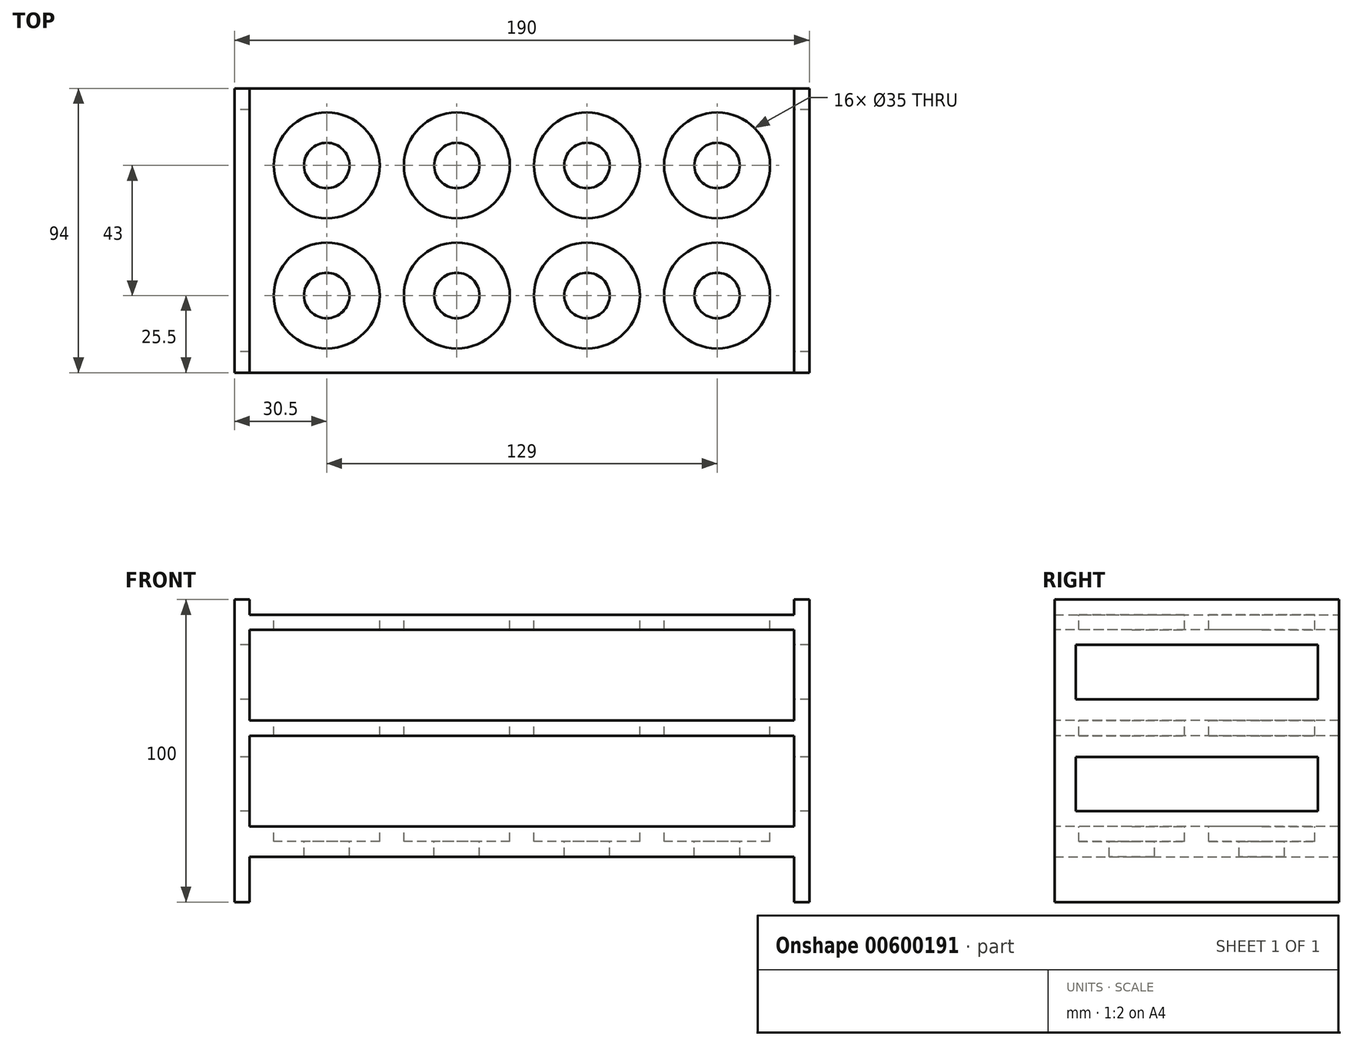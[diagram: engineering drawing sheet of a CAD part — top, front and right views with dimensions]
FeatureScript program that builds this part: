
annotation { "Feature Type Name" : "Feature", "Feature Type Description" : "" }
export const myFeature = defineFeature(function(context is Context, id is Id, definition is map)
    precondition{}
    {
        {
            var Q0;
            Q0=qCreatedBy(makeId("Top.planeOp"),FACE);
            var sketch = newSketch(context, id + "F0", { "sketchPlane" : qUnion([Q0])});
            skLineSegment(sketch, "E0.bottom", {"start": v(0, 0) * mm, "end": v(180, 0) * mm});
            skLineSegment(sketch, "E0.top", {"start": v(0, 94) * mm, "end": v(180, 94) * mm});
            skLineSegment(sketch, "E0.left", {"start": v(0, 0) * mm, "end": v(0, 94) * mm});
            skLineSegment(sketch, "E0.right", {"start": v(180, 0) * mm, "end": v(180, 94) * mm});
            skSolve(sketch);
        }
        {
            var Q0;
            Q0 = qSketchRegion(id + "F0", true);
            extrude(context, id + "F1", {"entities" : qUnion([Q0]), "depth" : 80 * mm, "offsetDistance" : 25 * mm});
        }
        {
            var Q0;
            Q0=makeQuery(id+"F1.opExtrude","CAP_FACE",FACE,{"disambiguationData":[OSD([sQuery(id+"F0.wireOp",EDGE,"E0.bottom"),sQuery(id+"F0.wireOp",EDGE,"E0.top"),sQuery(id+"F0.wireOp",EDGE,"E0.left"),sQuery(id+"F0.wireOp",EDGE,"E0.right")])],"isStart":false});
            var sketch = newSketch(context, id + "F2", { "sketchPlane" : qUnion([Q0])});
            skCircle(sketch, "E1", {"center": v(25.5, 25.5) * mm, "radius": 17.5 * mm});
            skCircle(sketch, "E2.0.1.0", {"center": v(25.5, 68.5) * mm, "radius": 17.5 * mm});
            skCircle(sketch, "E2.1.0.0", {"center": v(68.5, 25.5) * mm, "radius": 17.5 * mm});
            skCircle(sketch, "E2.1.1.0", {"center": v(68.5, 68.5) * mm, "radius": 17.5 * mm});
            skCircle(sketch, "E2.2.0.0", {"center": v(111.5, 25.5) * mm, "radius": 17.5 * mm});
            skCircle(sketch, "E2.2.1.0", {"center": v(111.5, 68.5) * mm, "radius": 17.5 * mm});
            skCircle(sketch, "E2.3.0.0", {"center": v(154.5, 25.5) * mm, "radius": 17.5 * mm});
            skCircle(sketch, "E2.3.1.0", {"center": v(154.5, 68.5) * mm, "radius": 17.5 * mm});
            skLineSegment(sketch, "E2.direction1", {"start": v(25.5, 25.5) * mm, "end": v(68.5, 25.5) * mm, "construction": true});
            skLineSegment(sketch, "E2.direction2", {"start": v(25.5, 25.5) * mm, "end": v(25.5, 68.5) * mm, "construction": true});
            skSolve(sketch);
        }
        {
            var Q0;
            Q0 = qSketchRegion(id + "F2", true);
            extrude(context, id + "F3", {"entities" : qUnion([Q0]), "operationType" : NewBodyOperationType.REMOVE, "oppositeDirection" : true, "depth" : 75 * mm, "offsetDistance" : 25 * mm});
        }
        {
            var Q0;
            Q0=makeQuery(id+"F1.opExtrude","SWEPT_FACE",FACE,{"disambiguationData":[OSD([sQuery(id+"F0.wireOp",EDGE,"E0.right")])]});
            var sketch = newSketch(context, id + "F4", { "sketchPlane" : qUnion([Q0])});
            skLineSegment(sketch, "E3.bottom", {"start": v(0, 75) * mm, "end": v(94, 75) * mm});
            skLineSegment(sketch, "E3.top", {"start": v(0, 45) * mm, "end": v(94, 45) * mm});
            skLineSegment(sketch, "E3.left", {"start": v(0, 75) * mm, "end": v(0, 45) * mm});
            skLineSegment(sketch, "E3.right", {"start": v(94, 75) * mm, "end": v(94, 45) * mm});
            skLineSegment(sketch, "E4.bottom", {"start": v(0, 40) * mm, "end": v(94, 40) * mm});
            skLineSegment(sketch, "E4.top", {"start": v(0, 10) * mm, "end": v(94, 10) * mm});
            skLineSegment(sketch, "E4.left", {"start": v(0, 40) * mm, "end": v(0, 10) * mm});
            skLineSegment(sketch, "E4.right", {"start": v(94, 40) * mm, "end": v(94, 10) * mm});
            skSolve(sketch);
        }
        {
            var Q0;
            Q0=makeQuery(id+"F4.imprint","IMPRINT",FACE,{"disambiguationData":[TD([[makeQuery(id+"F4.imprint","IMPRINT",EDGE,{"derivedFrom":sQuery(id+"F4.wireOp",EDGE,"E3.bottom")}),-1.0]])]});
            var Q1;
            Q1=makeQuery(id+"F4.imprint","IMPRINT",FACE,{"disambiguationData":[TD([[makeQuery(id+"F4.imprint","IMPRINT",EDGE,{"derivedFrom":sQuery(id+"F4.wireOp",EDGE,"E4.bottom")}),-1.0]])]});
            extrude(context, id + "F5", {"entities" : qUnion([Q0, Q1]), "operationType" : NewBodyOperationType.REMOVE, "endBound" : BoundingType.THROUGH_ALL, "oppositeDirection" : true, "depth" : 25 * mm, "offsetDistance" : 25 * mm});
        }
        {
            var Q0;
            {var subQ1=sQuery(id+"F0.wireOp",EDGE,"E0.left");Q0=makeQuery(id+"F5.boolean.opBoolean","SPLIT",FACE,{"disambiguationData":[TD([makeQuery(id+"F5.opExtrude","SWEPT_FACE",FACE,{"disambiguationData":[OSD([sQuery(id+"F4.wireOp",EDGE,"E3.bottom")])]})])],"derivedFrom":makeQuery(id+"F1.opExtrude","SWEPT_FACE",FACE,{"disambiguationData":[OSD([subQ1])]})});}
            var sketch = newSketch(context, id + "F6", { "sketchPlane" : qUnion([Q0])});
            skLineSegment(sketch, "E5.bottom", {"start": v(0, 85) * mm, "end": v(-94, 85) * mm});
            skLineSegment(sketch, "E5.top", {"start": v(0, -15) * mm, "end": v(-94, -15) * mm});
            skLineSegment(sketch, "E5.left", {"start": v(0, 85) * mm, "end": v(0, -15) * mm});
            skLineSegment(sketch, "E5.right", {"start": v(-94, 85) * mm, "end": v(-94, -15) * mm});
            skSolve(sketch);
        }
        {
            var Q0;
            Q0 = qSketchRegion(id + "F6", true);
            extrude(context, id + "F7", {"entities" : qUnion([Q0]), "operationType" : NewBodyOperationType.ADD, "depth" : 5 * mm, "offsetDistance" : 25 * mm});
        }
        {
            var Q0;
            {var subQ1=sQuery(id+"F0.wireOp",EDGE,"E0.right");Q0=makeQuery(id+"F5.boolean.opBoolean","SPLIT",FACE,{"disambiguationData":[TD([makeQuery(id+"F5.opExtrude","SWEPT_FACE",FACE,{"disambiguationData":[OSD([sQuery(id+"F4.wireOp",EDGE,"E3.bottom")])]})])],"derivedFrom":makeQuery(id+"F1.opExtrude","SWEPT_FACE",FACE,{"disambiguationData":[OSD([subQ1])]})});}
            var sketch = newSketch(context, id + "F8", { "sketchPlane" : qUnion([Q0])});
            skLineSegment(sketch, "E6.bottom", {"start": v(0, 85) * mm, "end": v(94, 85) * mm});
            skLineSegment(sketch, "E6.top", {"start": v(0, -15) * mm, "end": v(94, -15) * mm});
            skLineSegment(sketch, "E6.left", {"start": v(0, 85) * mm, "end": v(0, -15) * mm});
            skLineSegment(sketch, "E6.right", {"start": v(94, 85) * mm, "end": v(94, -15) * mm});
            skSolve(sketch);
        }
        {
            var Q0;
            Q0 = qSketchRegion(id + "F8", true);
            extrude(context, id + "F9", {"entities" : qUnion([Q0]), "operationType" : NewBodyOperationType.ADD, "depth" : 5 * mm, "offsetDistance" : 25 * mm});
        }
        {
            var Q0;
            Q0=makeQuery(id+"F3.boolean.opBoolean","COPY",FACE,{"derivedFrom":makeQuery(id+"F3.opExtrude","CAP_FACE",FACE,{"disambiguationData":[OSD([sQuery(id+"F2.wireOp",EDGE,"E1")])],"isStart":false})});
            var sketch = newSketch(context, id + "F10", { "sketchPlane" : qUnion([Q0])});
            skCircle(sketch, "E7", {"center": v(25.5, 25.5) * mm, "radius": 7.5 * mm});
            skCircle(sketch, "E8.0.1.0", {"center": v(25.5, 68.5) * mm, "radius": 7.5 * mm});
            skCircle(sketch, "E8.1.0.0", {"center": v(68.5, 25.5) * mm, "radius": 7.5 * mm});
            skCircle(sketch, "E8.1.1.0", {"center": v(68.5, 68.5) * mm, "radius": 7.5 * mm});
            skCircle(sketch, "E8.2.0.0", {"center": v(111.5, 25.5) * mm, "radius": 7.5 * mm});
            skCircle(sketch, "E8.2.1.0", {"center": v(111.5, 68.5) * mm, "radius": 7.5 * mm});
            skCircle(sketch, "E8.3.0.0", {"center": v(154.5, 25.5) * mm, "radius": 7.5 * mm});
            skCircle(sketch, "E8.3.1.0", {"center": v(154.5, 68.5) * mm, "radius": 7.5 * mm});
            skLineSegment(sketch, "E8.direction1", {"start": v(25.5, 25.5) * mm, "end": v(68.5, 25.5) * mm, "construction": true});
            skLineSegment(sketch, "E8.direction2", {"start": v(25.5, 25.5) * mm, "end": v(25.5, 68.5) * mm, "construction": true});
            skSolve(sketch);
        }
        {
            var Q0;
            Q0 = qSketchRegion(id + "F10", true);
            extrude(context, id + "F11", {"entities" : qUnion([Q0]), "operationType" : NewBodyOperationType.REMOVE, "oppositeDirection" : true, "depth" : 25 * mm, "offsetDistance" : 25 * mm});
        }
        {
            var Q0;
            {var subQ0=sQuery(id+"F8.wireOp",EDGE,"E6.right");var subQ1=sQuery(id+"F8.wireOp",EDGE,"E6.left");Q0=makeQuery(id+"F9.boolean.opBoolean","SPLIT",FACE,{"disambiguationData":[TD([makeQuery(id+"F5.boolean.opBoolean","COPY",FACE,{"derivedFrom":makeQuery(id+"F5.opExtrude","SWEPT_FACE",FACE,{"disambiguationData":[OSD([sQuery(id+"F4.wireOp",EDGE,"E3.bottom")])]})})])],"derivedFrom":makeQuery(id+"F9.opExtrude","CAP_FACE",FACE,{"disambiguationData":[OSD([sQuery(id+"F8.wireOp",EDGE,"E6.bottom"),sQuery(id+"F8.wireOp",EDGE,"E6.top"),subQ1,subQ0])],"isStart":true})});}
            var sketch = newSketch(context, id + "F12", { "sketchPlane" : qUnion([Q0])});
            skLineSegment(sketch, "E9.bottom", {"start": v(-87, 52) * mm, "end": v(-7, 52) * mm});
            skLineSegment(sketch, "E9.top", {"start": v(-87, 70) * mm, "end": v(-7, 70) * mm});
            skLineSegment(sketch, "E9.left", {"start": v(-87, 52) * mm, "end": v(-87, 70) * mm});
            skLineSegment(sketch, "E9.right", {"start": v(-7, 52) * mm, "end": v(-7, 70) * mm});
            skLineSegment(sketch, "E10.bottom", {"start": v(-87, 15) * mm, "end": v(-7, 15) * mm});
            skLineSegment(sketch, "E10.top", {"start": v(-87, 33) * mm, "end": v(-7, 33) * mm});
            skLineSegment(sketch, "E10.left", {"start": v(-87, 15) * mm, "end": v(-87, 33) * mm});
            skLineSegment(sketch, "E10.right", {"start": v(-7, 15) * mm, "end": v(-7, 33) * mm});
            skSolve(sketch);
        }
        {
            var Q0;
            Q0=makeQuery(id+"F12.imprint","IMPRINT",FACE,{"disambiguationData":[TD([[makeQuery(id+"F12.imprint","IMPRINT",EDGE,{"derivedFrom":sQuery(id+"F12.wireOp",EDGE,"E9.bottom")}),1.0]])]});
            var Q1;
            Q1=makeQuery(id+"F12.imprint","IMPRINT",FACE,{"disambiguationData":[TD([[makeQuery(id+"F12.imprint","IMPRINT",EDGE,{"derivedFrom":sQuery(id+"F12.wireOp",EDGE,"E10.bottom")}),1.0]])]});
            extrude(context, id + "F13", {"entities" : qUnion([Q0, Q1]), "operationType" : NewBodyOperationType.REMOVE, "endBound" : BoundingType.THROUGH_ALL, "oppositeDirection" : true, "depth" : 25 * mm, "offsetDistance" : 25 * mm, "hasSecondDirection" : true, "secondDirectionBound" : SecondDirectionBoundingType.THROUGH_ALL, "secondDirectionOppositeDirection" : false, "secondDirectionDepth" : 25 * mm});
        }
    });
